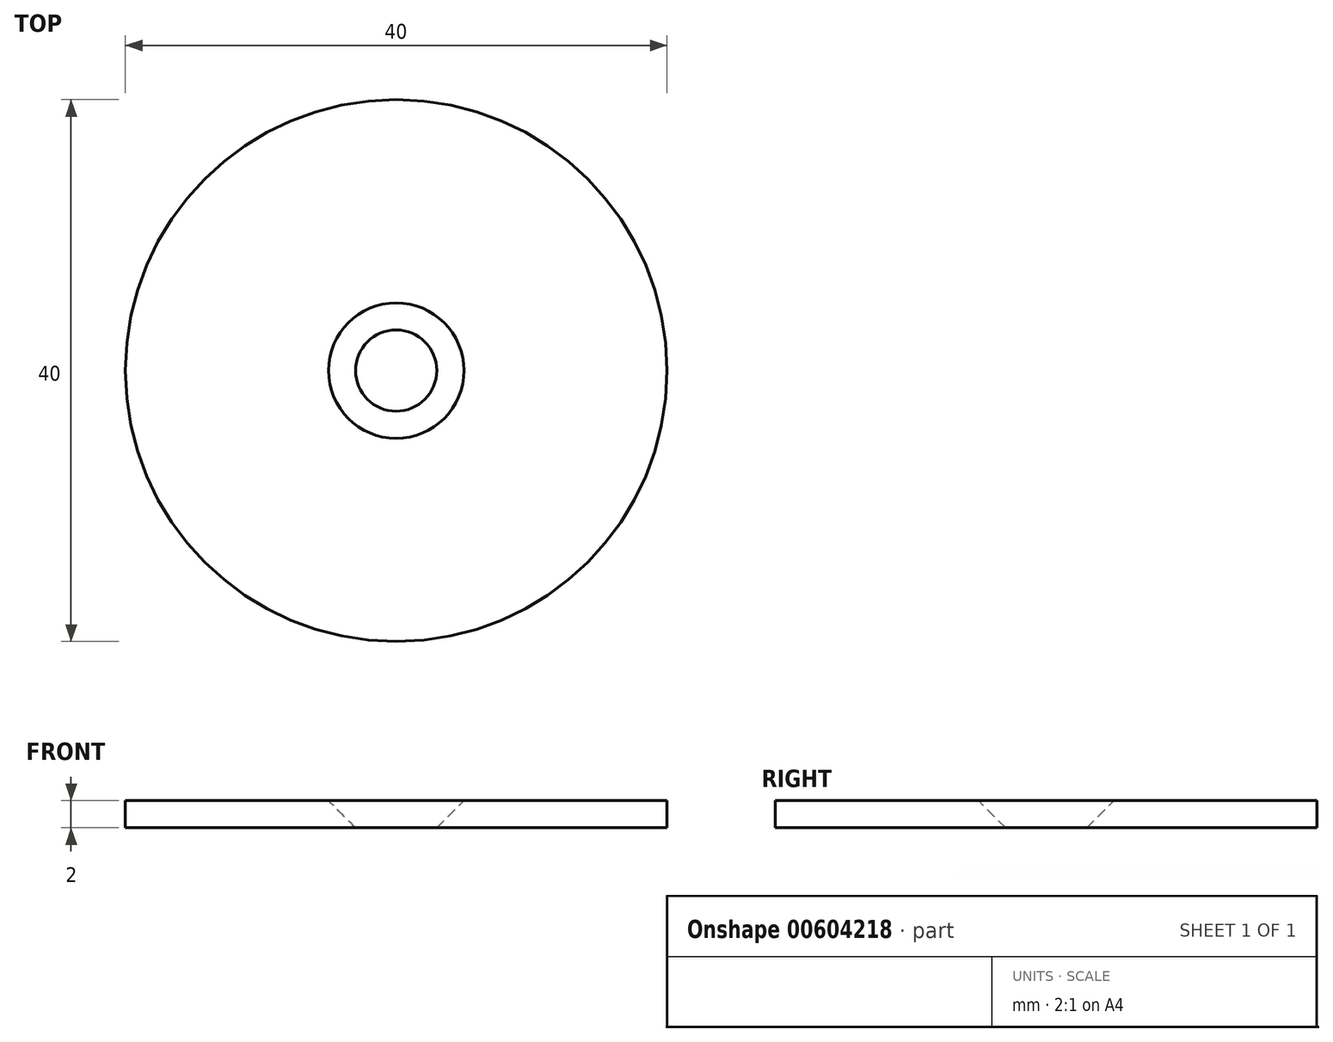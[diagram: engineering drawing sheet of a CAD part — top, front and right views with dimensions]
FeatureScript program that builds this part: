
annotation { "Feature Type Name" : "Feature", "Feature Type Description" : "" }
export const myFeature = defineFeature(function(context is Context, id is Id, definition is map)
    precondition{}
    {
        {
            var Q0;
            Q0=qCreatedBy(makeId("Front.planeOp"),FACE);
            var sketch = newSketch(context, id + "F0", { "sketchPlane" : qUnion([Q0])});
            skLineSegment(sketch, "E0", {"start": v(3, 0) * mm, "end": v(20, 0) * mm});
            skLineSegment(sketch, "E1", {"start": v(20, 0) * mm, "end": v(20, 2) * mm});
            skLineSegment(sketch, "E2", {"start": v(20, 2) * mm, "end": v(5, 2) * mm});
            skLineSegment(sketch, "E3", {"start": v(5, 2) * mm, "end": v(3, 0) * mm});
            skLineSegment(sketch, "E4", {"start": v(0, 0) * mm, "end": v(0, 17.8) * mm, "construction": true});
            skSolve(sketch);
        }
        {
            var Q0;
            Q0=makeQuery(id+"F0.imprint","IMPRINT",FACE,{"disambiguationData":[TD([[makeQuery(id+"F0.imprint","IMPRINT",EDGE,{"derivedFrom":sQuery(id+"F0.wireOp",EDGE,"E0")}),1.0]])]});
            var Q1;
            Q1=sQuery(id+"F0.wireOp",EDGE,"E4");
            revolve(context, id + "F1", {"entities" : qUnion([Q0]), "axis" : qUnion([Q1]), "revolveType" : RevolveType.FULL});
        }
    });
